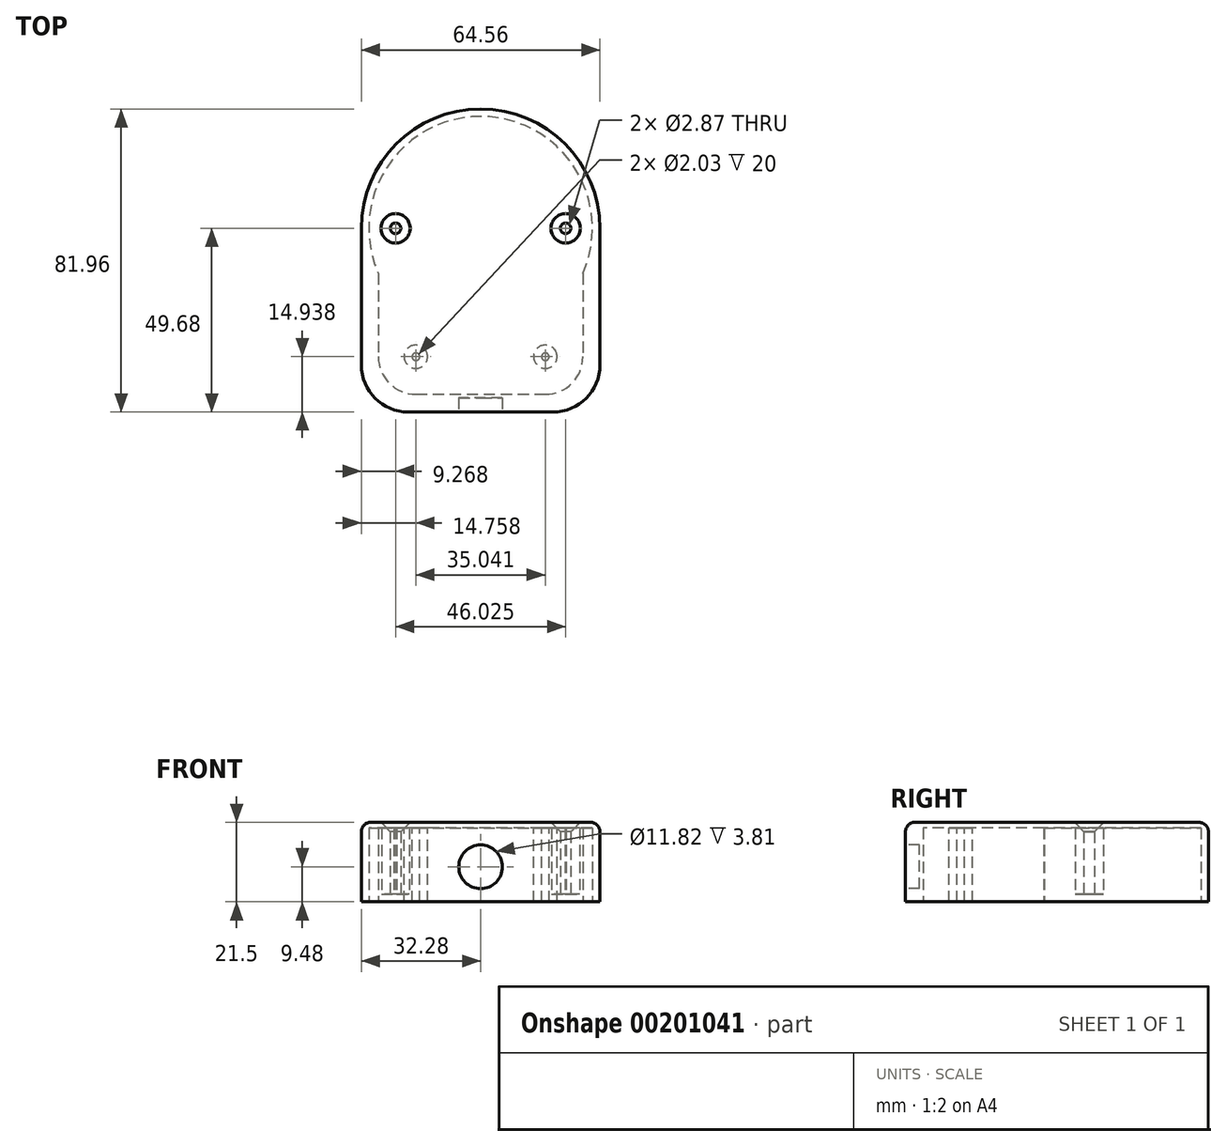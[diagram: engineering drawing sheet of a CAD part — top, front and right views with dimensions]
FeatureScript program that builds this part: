
annotation { "Feature Type Name" : "Feature", "Feature Type Description" : "" }
export const myFeature = defineFeature(function(context is Context, id is Id, definition is map)
    precondition{}
    {
        {
            var Q0;
            Q0=qCreatedBy(makeId("Top.planeOp"),FACE);
            var sketch = newSketch(context, id + "F0", { "sketchPlane" : qUnion([Q0])});
            skArc(sketch, "E0.0", {"start": v(32.28, 0) * mm, "mid": v(0, 32.28) * mm, "end": v(-32.28, 0) * mm});
            skLineSegment(sketch, "E1.left", {"start": v(32.28, 0) * mm, "end": v(32.28, 0) * mm});
            skLineSegment(sketch, "E1.right", {"start": v(-32.28, 0) * mm, "end": v(-32.28, 0) * mm});
            skLineSegment(sketch, "E2", {"start": v(-32.28, 0) * mm, "end": v(-32.28, -36.98) * mm});
            skLineSegment(sketch, "E3", {"start": v(-19.58, -49.68) * mm, "end": v(19.58, -49.68) * mm});
            skLineSegment(sketch, "E4", {"start": v(32.28, -36.98) * mm, "end": v(32.28, 0) * mm});
            skPoint(sketch, "E5.visualSharp", {"position": v(-32.28, -49.68) * mm});
            skArc(sketch, "E5.filletArc", {"start": v(-32.28, -36.98) * mm, "mid": v(-28.56, -45.96) * mm, "end": v(-19.58, -49.68) * mm});
            skPoint(sketch, "E6.visualSharp", {"position": v(32.28, -49.68) * mm});
            skArc(sketch, "E6.filletArc", {"start": v(19.58, -49.68) * mm, "mid": v(28.56, -45.96) * mm, "end": v(32.28, -36.98) * mm});
            skSolve(sketch);
        }
        {
            var Q0;
            Q0=qCreatedBy(makeId("Top.planeOp"),FACE);
            var sketch = newSketch(context, id + "F1", { "sketchPlane" : qUnion([Q0])});
            skArc(sketch, "E7", {"start": v(14.39, 5.75) * mm, "mid": v(0, 15.5) * mm, "end": v(-14.39, 5.75) * mm});
            skLineSegment(sketch, "E8.top", {"start": v(14.39, -27.89) * mm, "end": v(-14.39, -27.89) * mm});
            skLineSegment(sketch, "E8.left", {"start": v(14.39, 5.75) * mm, "end": v(14.39, -27.89) * mm});
            skLineSegment(sketch, "E8.right", {"start": v(-14.39, 5.75) * mm, "end": v(-14.39, -27.89) * mm});
            skPoint(sketch, "E9.orphan", {"position": v(-14.39, 15.5) * mm});
            skCircle(sketch, "E10", {"center": v(0, 0) * mm, "radius": 7.62 * mm});
            skLineSegment(sketch, "E11", {"start": v(-2.22, -34.24) * mm, "end": v(10.48, -34.24) * mm});
            skSolve(sketch);
        }
        {
            var Q0;
            Q0 = qSketchRegion(id + "F1", true);
            extrude(context, id + "F2", {"entities" : qUnion([Q0]), "depth" : 9 * mm});
        }
        {
            var Q0;
            Q0=qCreatedBy(makeId("Top.planeOp"),FACE);
            var sketch = newSketch(context, id + "F3", { "sketchPlane" : qUnion([Q0])});
            skCircle(sketch, "E12", {"center": v(0, 0) * mm, "radius": 3.18 * mm});
            skSolve(sketch);
        }
        {
            var Q0;
            Q0 = qSketchRegion(id + "F3", true);
            var Q1;
            Q1 = qSketchRegion(id + "F5", true);
            extrude(context, id + "F4", {"entities" : qUnion([Q0, Q1]), "depth" : 18.5 * mm});
        }
        {
            var Q0;
            Q0=qCreatedBy(makeId("Top.planeOp"),FACE);
            var sketch = newSketch(context, id + "F5", { "sketchPlane" : qUnion([Q0])});
            skCircle(sketch, "E13", {"center": v(-23.01, 0) * mm, "radius": 1.44 * mm});
            skCircle(sketch, "E14", {"center": v(23.01, 0) * mm, "radius": 1.44 * mm});
            skSolve(sketch);
        }
        {
            var Q0;
            Q0=qCreatedBy(makeId("Top.planeOp"),FACE);
            var sketch = newSketch(context, id + "F6", { "sketchPlane" : qUnion([Q0])});
            skCircle(sketch, "E15", {"center": v(0, 0) * mm, "radius": 30.25 * mm});
            skSolve(sketch);
        }
        {
            var Q0;
            Q0 = qSketchRegion(id + "F0", true);
            extrude(context, id + "F7", {"entities" : qUnion([Q0]), "depth" : 21.5 * mm});
        }
        {
            var Q0;
            Q0 = qSketchRegion(id + "F5", true);
            extrude(context, id + "F8", {"entities" : qUnion([Q0]), "operationType" : NewBodyOperationType.REMOVE, "depth" : 25.4 * mm});
        }
        {
            var Q0;
            Q0=qCreatedBy(makeId("Top.planeOp"),FACE);
            var sketch = newSketch(context, id + "F9", { "sketchPlane" : qUnion([Q0])});
            skCircle(sketch, "E16", {"center": v(0, 0) * mm, "radius": 30.25 * mm});
            skCircle(sketch, "E17", {"center": v(23.01, 0) * mm, "radius": 3.81 * mm});
            skCircle(sketch, "E18", {"center": v(-23.01, 0) * mm, "radius": 3.81 * mm});
            skSolve(sketch);
        }
        {
            var Q0;
            Q0=qCreatedBy(makeId("Top.planeOp"),FACE);
            var sketch = newSketch(context, id + "F10", { "sketchPlane" : qUnion([Q0])});
            skArc(sketch, "E19", {"start": v(-27.68, -3.79) * mm, "mid": v(-0.01, -27.94) * mm, "end": v(27.68, -3.8) * mm});
            skArc(sketch, "E20", {"start": v(23.11, 3.8) * mm, "mid": v(19.15, 0.05) * mm, "end": v(23.02, -3.8) * mm});
            skArc(sketch, "E21", {"start": v(-23.5, -3.79) * mm, "mid": v(-19.29, 0) * mm, "end": v(-23.5, 3.79) * mm});
            skLineSegment(sketch, "E22", {"start": v(22.81, 3.8) * mm, "end": v(27.68, 3.8) * mm});
            skLineSegment(sketch, "E23", {"start": v(23.02, -3.8) * mm, "end": v(27.68, -3.8) * mm});
            skLineSegment(sketch, "E24", {"start": v(-23.5, 3.79) * mm, "end": v(-27.68, 3.79) * mm});
            skLineSegment(sketch, "E25", {"start": v(-22.69, -3.79) * mm, "end": v(-27.68, -3.79) * mm});
            skArc(sketch, "E26.trimOffspring", {"start": v(27.68, 3.8) * mm, "mid": v(0, 27.94) * mm, "end": v(-27.68, 3.79) * mm});
            skLineSegment(sketch, "E27", {"start": v(-17.52, -44.9) * mm, "end": v(17.52, -44.9) * mm});
            skPoint(sketch, "E28.start.orphan", {"position": v(27.68, -37) * mm});
            skLineSegment(sketch, "E29", {"start": v(-27.68, -3.79) * mm, "end": v(-27.68, -34.74) * mm});
            skLineSegment(sketch, "E30", {"start": v(27.68, -3.8) * mm, "end": v(27.68, -34.74) * mm});
            skPoint(sketch, "E31.visualSharp", {"position": v(-27.68, -44.9) * mm});
            skArc(sketch, "E31.filletArc", {"start": v(-27.68, -34.74) * mm, "mid": v(-24.7, -41.93) * mm, "end": v(-17.52, -44.9) * mm});
            skPoint(sketch, "E32.visualSharp", {"position": v(27.68, -44.9) * mm});
            skArc(sketch, "E32.filletArc", {"start": v(17.52, -44.9) * mm, "mid": v(24.7, -41.93) * mm, "end": v(27.68, -34.74) * mm});
            skSolve(sketch);
        }
        {
            var Q0;
            Q0 = qSketchRegion(id + "F10", true);
            extrude(context, id + "F11", {"entities" : qUnion([Q0]), "operationType" : NewBodyOperationType.REMOVE, "depth" : 20 * mm});
        }
        {
            var Q0;
            Q0=makeQuery(id+"F7.opExtrude","CAP_EDGE",EDGE,{"disambiguationData":[OSD([sQuery(id+"F0.wireOp",EDGE,"E0.0")])],"isStart":false});
            fillet(context, id + "F12", {"entities" : qUnion([Q0]), "radius" : 2.54 * mm, "tangentPropagation" : true, "allowEdgeOverflow" : false});
        }
        {
            var Q0;
            Q0=makeQuery(id+"F8.boolean.opBoolean","INTERSECT",EDGE,{"derivedFrom":[makeQuery(id+"F7.opExtrude","CAP_FACE",FACE,{"disambiguationData":[OSD([sQuery(id+"F0.wireOp",EDGE,"E0.0")])],"isStart":false}),makeQuery(id+"F8.opExtrude","SWEPT_FACE",FACE,{"disambiguationData":[OSD([sQuery(id+"F5.wireOp",EDGE,"E13")])]})]});
            var Q1;
            Q1=makeQuery(id+"F8.boolean.opBoolean","INTERSECT",EDGE,{"derivedFrom":[makeQuery(id+"F7.opExtrude","CAP_FACE",FACE,{"disambiguationData":[OSD([sQuery(id+"F0.wireOp",EDGE,"E0.0")])],"isStart":false}),makeQuery(id+"F8.opExtrude","SWEPT_FACE",FACE,{"disambiguationData":[OSD([sQuery(id+"F5.wireOp",EDGE,"E14")])]})]});
            chamfer(context, id + "F13", {"entities" : qUnion([Q0, Q1]), "width" : 2.54 * mm, "tangentPropagation" : true});
        }
        {
            var Q0;
            Q0 = qSketchRegion(id + "F6", true);
            extrude(context, id + "F14", {"entities" : qUnion([Q0]), "operationType" : NewBodyOperationType.REMOVE, "depth" : 2.03 * mm});
        }
        {
            var Q0;
            Q0 = qSketchRegion(id + "F9", true);
            extrude(context, id + "F15", {"entities" : qUnion([Q0]), "operationType" : NewBodyOperationType.REMOVE, "depth" : 20 * mm});
        }
        {
            var Q0;
            Q0=qCreatedBy(makeId("Top.planeOp"),FACE);
            var sketch = newSketch(context, id + "F16", { "sketchPlane" : qUnion([Q0])});
            skCircle(sketch, "E33", {"center": v(0, 0) * mm, "radius": 30.25 * mm});
            skSolve(sketch);
        }
        {
            var Q0;
            Q0 = qSketchRegion(id + "F16", true);
            var Q1;
            Q1 = qSketchRegion(id + "F6", true);
            extrude(context, id + "F17", {"entities" : qUnion([Q0, Q1]), "operationType" : NewBodyOperationType.REMOVE, "depth" : 2.03 * mm});
        }
        {
            var Q0;
            Q0=makeQuery(id+"F7.opExtrude","SWEPT_FACE",FACE,{"disambiguationData":[OSD([sQuery(id+"F0.wireOp",EDGE,"E3")])]});
            var sketch = newSketch(context, id + "F18", { "sketchPlane" : qUnion([Q0])});
            skCircle(sketch, "E34", {"center": v(0, 9.48) * mm, "radius": 5.9 * mm});
            skPoint(sketch, "E34.centerSnap0", {"position": v(0, 18.96) * mm});
            skPoint(sketch, "E34.centerSnap1", {"position": v(19.58, 9.48) * mm});
            skSolve(sketch);
        }
        {
            var Q0;
            Q0 = qSketchRegion(id + "F18", true);
            extrude(context, id + "F19", {"entities" : qUnion([Q0]), "operationType" : NewBodyOperationType.REMOVE, "oppositeDirection" : true, "depth" : 3.8 * mm});
        }
        {
            var Q0;
            Q0=makeQuery(id+"F11.boolean.opBoolean","COPY",FACE,{"derivedFrom":makeQuery(id+"F11.opExtrude","CAP_FACE",FACE,{"disambiguationData":[OSD([sQuery(id+"F10.wireOp",EDGE,"E20"),sQuery(id+"F10.wireOp",EDGE,"E21"),sQuery(id+"F10.wireOp",EDGE,"E22"),sQuery(id+"F10.wireOp",EDGE,"E23"),sQuery(id+"F10.wireOp",EDGE,"E24"),sQuery(id+"F10.wireOp",EDGE,"E25"),sQuery(id+"F10.wireOp",EDGE,"E26.trimOffspring"),sQuery(id+"F10.wireOp",EDGE,"E27"),sQuery(id+"F10.wireOp",EDGE,"E29"),sQuery(id+"F10.wireOp",EDGE,"E30"),sQuery(id+"F10.wireOp",EDGE,"E31.filletArc"),sQuery(id+"F10.wireOp",EDGE,"E32.filletArc")])],"isStart":false})});
            var sketch = newSketch(context, id + "F20", { "sketchPlane" : qUnion([Q0])});
            skCircle(sketch, "E35", {"center": v(17.52, 34.74) * mm, "radius": 3.18 * mm});
            skCircle(sketch, "E36", {"center": v(-17.52, 34.74) * mm, "radius": 3.18 * mm});
            skCircle(sketch, "E37", {"center": v(17.52, 34.74) * mm, "radius": 1.02 * mm});
            skCircle(sketch, "E38", {"center": v(-17.52, 34.74) * mm, "radius": 1.02 * mm});
            skSolve(sketch);
        }
        {
            var Q0;
            Q0 = qSketchRegion(id + "F20", true);
            var Q1;
            Q1=makeQuery(id+"F7.opExtrude","CAP_FACE",FACE,{"disambiguationData":[OSD([sQuery(id+"F0.wireOp",EDGE,"E0.0"),sQuery(id+"F0.wireOp",EDGE,"E2"),sQuery(id+"F0.wireOp",EDGE,"E3"),sQuery(id+"F0.wireOp",EDGE,"E4"),sQuery(id+"F0.wireOp",EDGE,"E5.filletArc"),sQuery(id+"F0.wireOp",EDGE,"E6.filletArc")])],"isStart":true});
            extrude(context, id + "F21", {"entities" : qUnion([Q0]), "operationType" : NewBodyOperationType.ADD, "endBound" : BoundingType.UP_TO_SURFACE, "endBoundEntityFace" : qUnion([Q1]), "depth" : 25.4 * mm});
        }
    });
